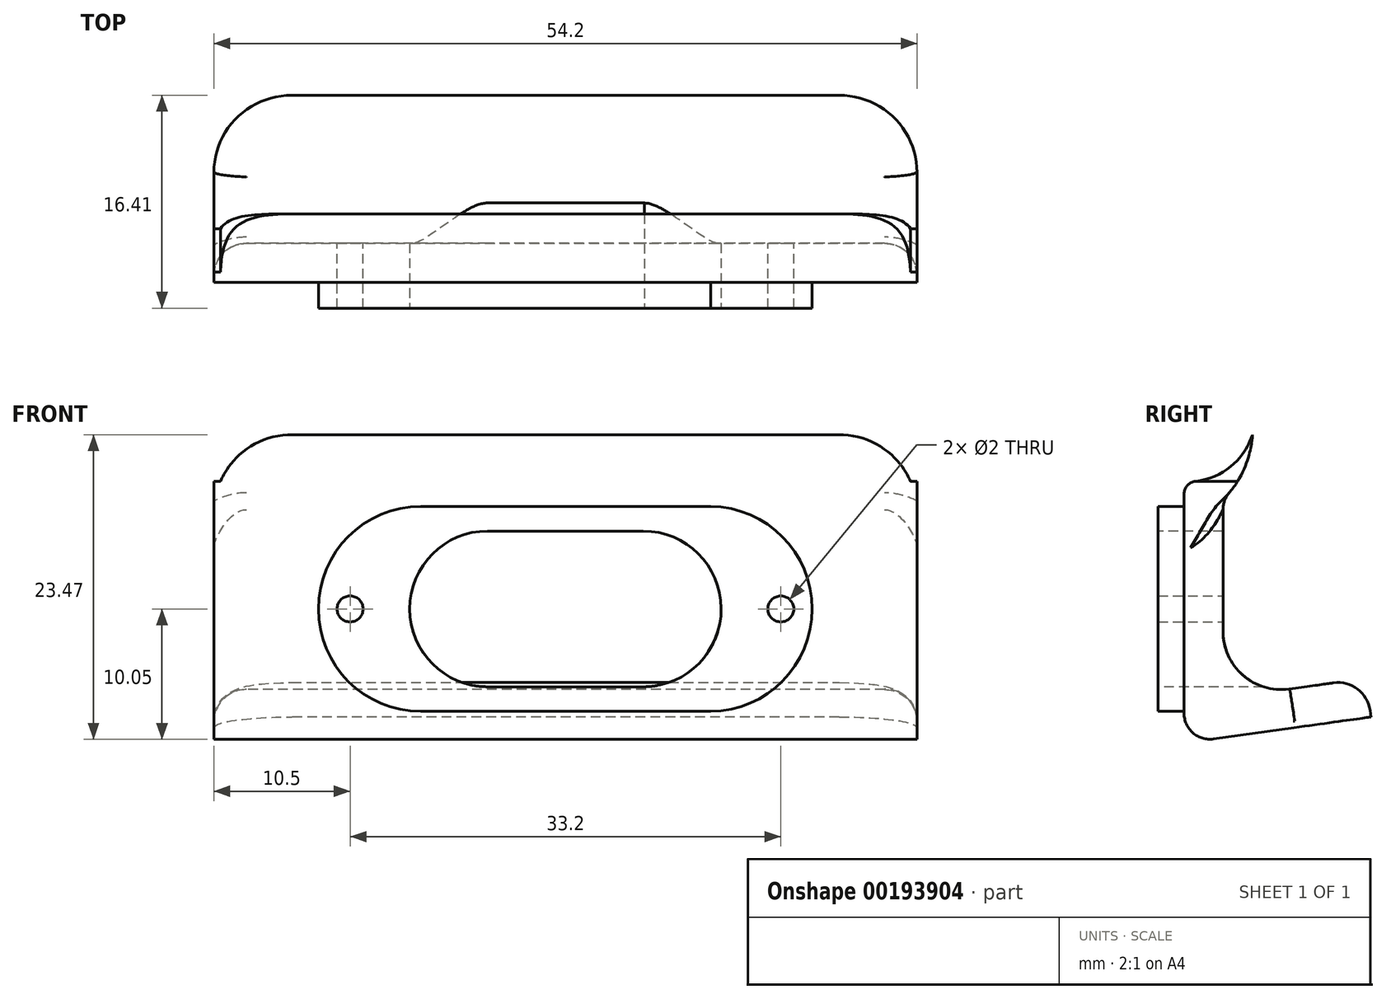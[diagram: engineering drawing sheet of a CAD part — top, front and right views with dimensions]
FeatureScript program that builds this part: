
annotation { "Feature Type Name" : "Feature", "Feature Type Description" : "" }
export const myFeature = defineFeature(function(context is Context, id is Id, definition is map)
    precondition{}
    {
        {
            var Q0;
            Q0=qCreatedBy(makeId("Front.planeOp"),FACE);
            var sketch = newSketch(context, id + "F0", { "sketchPlane" : qUnion([Q0])});
            skLineSegment(sketch, "E0", {"start": v(-6, -6) * mm, "end": v(6.1, -6) * mm});
            skPoint(sketch, "E1.endSnap0", {"position": v(0.05, -6) * mm});
            skArc(sketch, "E2", {"start": v(-11.14, 7.9) * mm, "mid": v(-19.04, 0) * mm, "end": v(-11.14, -7.9) * mm});
            skArc(sketch, "E3", {"start": v(11.2, -7.9) * mm, "mid": v(19.02, 0) * mm, "end": v(11.2, 7.9) * mm});
            skLineSegment(sketch, "E4", {"start": v(-11.14, 7.9) * mm, "end": v(11.2, 7.9) * mm});
            skLineSegment(sketch, "E5", {"start": v(-11.14, -7.9) * mm, "end": v(11.2, -7.9) * mm});
            skPoint(sketch, "E6", {"position": v(0.03, 7.9) * mm});
            skPoint(sketch, "E7", {"position": v(0, 15.9) * mm});
            skPoint(sketch, "E8", {"position": v(0.05, -7.9) * mm});
            skPoint(sketch, "E9", {"position": v(0.05, -10.36) * mm});
            skPoint(sketch, "E10", {"position": v(19.02, 0) * mm});
            skPoint(sketch, "E11", {"position": v(27.02, 0) * mm});
            skPoint(sketch, "E12", {"position": v(-19.04, 0) * mm});
            skPoint(sketch, "E13", {"position": v(-27.04, 0) * mm});
            skLineSegment(sketch, "E14", {"start": v(27.02, 0) * mm, "end": v(11.12, 0) * mm, "construction": true});
            skLineSegment(sketch, "E15", {"start": v(-27.04, 0) * mm, "end": v(-11.14, 0) * mm, "construction": true});
            skLineSegment(sketch, "E16", {"start": v(27.02, 0) * mm, "end": v(27.02, -10.36) * mm});
            skLineSegment(sketch, "E17", {"start": v(27.02, -10.36) * mm, "end": v(0.05, -10.36) * mm});
            skLineSegment(sketch, "E18", {"start": v(-27.04, 0) * mm, "end": v(-27.04, -10.36) * mm});
            skLineSegment(sketch, "E19", {"start": v(-27.04, -10.36) * mm, "end": v(0.05, -10.36) * mm});
            skLineSegment(sketch, "E20", {"start": v(-6, -6) * mm, "end": v(-6, 6) * mm, "construction": true});
            skArc(sketch, "E21", {"start": v(-6, 6) * mm, "mid": v(-12, 0) * mm, "end": v(-6, -6) * mm});
            skLineSegment(sketch, "E22", {"start": v(6, 6) * mm, "end": v(-6, 6) * mm});
            skArc(sketch, "E23", {"start": v(6.1, -6) * mm, "mid": v(12, 0.05) * mm, "end": v(6, 6) * mm});
            skLineSegment(sketch, "E24", {"start": v(0, 2.4) * mm, "end": v(16.6, 2.4) * mm, "construction": true});
            skLineSegment(sketch, "E25", {"start": v(16.6, 2.4) * mm, "end": v(16.6, 0) * mm, "construction": true});
            skLineSegment(sketch, "E26.MirrorCS", {"start": v(16.6, 2.4) * mm, "end": v(16.6, 4.8) * mm, "construction": true});
            skLineSegment(sketch, "E27.MirrorCS", {"start": v(-16.6, 2.4) * mm, "end": v(-16.6, 0) * mm, "construction": true});
            skCircle(sketch, "E28", {"center": v(-16.6, 0) * mm, "radius": 1 * mm});
            skCircle(sketch, "E29", {"center": v(16.6, 0) * mm, "radius": 1 * mm});
            skPoint(sketch, "E30.0.midPoint", {"position": v(16.6, -2.75) * mm});
            skPoint(sketch, "E31.0.midPoint", {"position": v(-16.6, -2.75) * mm});
            skSolve(sketch);
        }
        {
            var Q0;
            Q0=qCreatedBy(makeId("Right.planeOp"),FACE);
            var sketch = newSketch(context, id + "F1", { "sketchPlane" : qUnion([Q0])});
            skPoint(sketch, "E32", {"position": v(-15.3, 23.66) * mm});
            skLineSegment(sketch, "E33", {"start": v(0, 0) * mm, "end": v(16.18, 0) * mm, "construction": true});
            skLineSegment(sketch, "E34", {"start": v(16.18, 0) * mm, "end": v(16.18, 14.83) * mm, "construction": true});
            skLineSegment(sketch, "E35", {"start": v(16.18, 14.83) * mm, "end": v(-20.13, 14.83) * mm, "construction": true});
            skLineSegment(sketch, "E36", {"start": v(0, 19.1) * mm, "end": v(0.5, 19.1) * mm, "construction": true});
            skLineSegment(sketch, "E37", {"start": v(0.5, 19.1) * mm, "end": v(0.5, 14.83) * mm, "construction": true});
            skArc(sketch, "E38", {"start": v(0.5, 9.83) * mm, "mid": v(0.68, 9.83) * mm, "end": v(0.86, 9.84) * mm});
            skArc(sketch, "E39", {"start": v(0, 9.83) * mm, "mid": v(3.82, 11.16) * mm, "end": v(5.5, 14.83) * mm});
            skLineSegment(sketch, "E40", {"start": v(0, 9.83) * mm, "end": v(0, 7.9) * mm});
            skLineSegment(sketch, "E41", {"start": v(0, 7.9) * mm, "end": v(-2, 7.9) * mm});
            skLineSegment(sketch, "E42", {"start": v(-2, 7.9) * mm, "end": v(-2, 5.99) * mm});
            skArc(sketch, "E43.trimOffspring", {"start": v(5.5, 14.83) * mm, "mid": v(5.43, 15.63) * mm, "end": v(5.24, 16.41) * mm});
            skLineSegment(sketch, "E44", {"start": v(0, 9.83) * mm, "end": v(0.5, 9.83) * mm});
            skCircle(sketch, "E45", {"center": v(0.35, 14.97) * mm, "radius": 5.15 * mm, "construction": true});
            skLineSegment(sketch, "E46", {"start": v(0, 0) * mm, "end": v(0, -3.97) * mm});
            skPoint(sketch, "E47.visualSharp", {"position": v(0, -10.35) * mm});
            skLineSegment(sketch, "E48", {"start": v(3, -9.92) * mm, "end": v(14.41, -8.32) * mm});
            skPoint(sketch, "E49.visualSharp", {"position": v(14, -5.35) * mm});
            skLineSegment(sketch, "E50", {"start": v(3, -6.9) * mm, "end": v(3, 0) * mm});
            skPoint(sketch, "E51.start.orphan", {"position": v(0, -7.85) * mm});
            skLineSegment(sketch, "E52", {"start": v(3, -9.92) * mm, "end": v(0, -10.35) * mm});
            skLineSegment(sketch, "E53", {"start": v(0, -10.35) * mm, "end": v(0, -7.85) * mm});
            skLineSegment(sketch, "E54", {"start": v(0, -7.85) * mm, "end": v(0, 0) * mm});
            skLineSegment(sketch, "E55", {"start": v(0, 0) * mm, "end": v(3, 0) * mm});
            skLineSegment(sketch, "E56", {"start": v(3, -6.9) * mm, "end": v(14, -5.35) * mm});
            skLineSegment(sketch, "E57", {"start": v(14.41, -8.32) * mm, "end": v(14, -5.35) * mm});
            skLineSegment(sketch, "E58", {"start": v(0, 0) * mm, "end": v(3, 0) * mm, "construction": true});
            skLineSegment(sketch, "E59", {"start": v(0.5, 9.83) * mm, "end": v(0.5, 6.83) * mm, "construction": true});
            skPoint(sketch, "E60", {"position": v(5.27, 13.43) * mm});
            skArc(sketch, "E61", {"start": v(0.5, 6.83) * mm, "mid": v(0.68, 6.9) * mm, "end": v(0.87, 6.98) * mm});
            skLineSegment(sketch, "E62", {"start": v(3, 0) * mm, "end": v(3, 8.44) * mm});
            skArc(sketch, "E63.trimOffspring", {"start": v(3, 8.44) * mm, "mid": v(4.6, 10.72) * mm, "end": v(5.27, 13.43) * mm});
            skLineSegment(sketch, "E64", {"start": v(0, 7.9) * mm, "end": v(0, 0) * mm});
            skSolve(sketch);
        }
        {
            var Q0;
            Q0=makeQuery(id+"F1.imprint","IMPRINT",FACE,{"disambiguationData":[TD([[makeQuery(id+"F1.imprint","IMPRINT",EDGE,{"derivedFrom":sQuery(id+"F1.wireOp",EDGE,"E48")}),1.0]])]});
            var Q1;
            {var subQ5=sQuery(id+"F1.wireOp",EDGE,"E40");Q1=makeQuery(id+"F1.imprint","IMPRINT",FACE,{"disambiguationData":[TD([[makeQuery(id+"F1.imprint","IMPRINT",EDGE,{"derivedFrom":subQ5}),1.0]])]});}
            extrude(context, id + "F2", {"entities" : qUnion([Q0, Q1]), "endBound" : BoundingType.SYMMETRIC, "depth" : 54.2 * mm});
        }
        {
            var Q0;
            Q0=makeQuery(id+"F0.imprint","IMPRINT",FACE,{"disambiguationData":[TD([[makeQuery(id+"F0.imprint","IMPRINT",EDGE,{"derivedFrom":sQuery(id+"F0.wireOp",EDGE,"E0")}),1.0]])]});
            extrude(context, id + "F3", {"entities" : qUnion([Q0]), "operationType" : NewBodyOperationType.ADD, "oppositeDirection" : true, "depth" : 3 * mm});
        }
        {
            var Q0;
            Q0=makeQuery(id+"F0.imprint","IMPRINT",FACE,{"disambiguationData":[TD([[makeQuery(id+"F0.imprint","IMPRINT",EDGE,{"derivedFrom":sQuery(id+"F0.wireOp",EDGE,"E0")}),1.0]])]});
            extrude(context, id + "F4", {"entities" : qUnion([Q0]), "operationType" : NewBodyOperationType.REMOVE, "oppositeDirection" : true, "depth" : 3 * mm});
        }
        {
            var Q0;
            Q0=makeQuery(id+"F0.imprint","IMPRINT",FACE,{"disambiguationData":[TD([[makeQuery(id+"F0.imprint","IMPRINT",EDGE,{"derivedFrom":sQuery(id+"F0.wireOp",EDGE,"E0")}),-1.0]])]});
            extrude(context, id + "F5", {"entities" : qUnion([Q0]), "operationType" : NewBodyOperationType.ADD, "depth" : 2 * mm});
        }
        {
            var Q0;
            Q0=makeQuery(id+"F2.opExtrude","SWEPT_EDGE",EDGE,{"disambiguationData":[OSD([sQuery(id+"F1.wireOp",EDGE,"E50"),sQuery(id+"F1.wireOp",EDGE,"E56")])]});
            var Q1;
            Q1=makeQuery(id+"F4.boolean.opBoolean","COPY",EDGE,{"derivedFrom":makeQuery(id+"F4.opExtrude","CAP_EDGE",EDGE,{"disambiguationData":[OSD([sQuery(id+"F0.wireOp",EDGE,"E22")])],"isStart":false})});
            fillet(context, id + "F6", {"entities" : qUnion([Q0, Q1]), "radius" : 4.5 * mm, "tangentPropagation" : true, "allowEdgeOverflow" : false});
        }
        {
            var Q0;
            Q0=makeQuery(id+"F2.opExtrude","SWEPT_FACE",FACE,{"disambiguationData":[OSD([sQuery(id+"F1.wireOp",EDGE,"E48"),sQuery(id+"F1.wireOp",EDGE,"E52")])]});
            var sketch = newSketch(context, id + "F7", { "sketchPlane" : qUnion([Q0])});
            skLineSegment(sketch, "E65", {"start": v(27.1, -7.11) * mm, "end": v(27.1, -7.11) * mm});
            skLineSegment(sketch, "E66", {"start": v(21.1, -13.11) * mm, "end": v(21.1, -13.11) * mm});
            skLineSegment(sketch, "E67", {"start": v(27.1, -7.11) * mm, "end": v(21.1, -7.11) * mm, "construction": true});
            skPoint(sketch, "E68.visualSharp", {"position": v(27.1, -13.11) * mm});
            skArc(sketch, "E68.filletArc", {"start": v(21.1, -13.11) * mm, "mid": v(25.34, -11.36) * mm, "end": v(27.1, -7.11) * mm});
            skLineSegment(sketch, "E69", {"start": v(27.1, -7.11) * mm, "end": v(27.1, -13.11) * mm});
            skLineSegment(sketch, "E70", {"start": v(21.1, -13.11) * mm, "end": v(27.1, -13.11) * mm});
            skLineSegment(sketch, "E71", {"start": v(-27.1, -7.11) * mm, "end": v(-27.1, -7.11) * mm});
            skLineSegment(sketch, "E72", {"start": v(-21.1, -13.11) * mm, "end": v(-21.1, -13.11) * mm});
            skLineSegment(sketch, "E73", {"start": v(-21.1, -13.11) * mm, "end": v(-21.1, -7.11) * mm, "construction": true});
            skLineSegment(sketch, "E74", {"start": v(-21.1, -7.11) * mm, "end": v(-27.1, -7.11) * mm, "construction": true});
            skPoint(sketch, "E75.visualSharp", {"position": v(-27.1, -13.11) * mm});
            skArc(sketch, "E75.filletArc", {"start": v(-27.1, -7.11) * mm, "mid": v(-25.34, -11.36) * mm, "end": v(-21.1, -13.11) * mm});
            skSolve(sketch);
        }
        {
            var Q0;
            Q0=makeQuery(id+"F7.imprint","IMPRINT",FACE,{"disambiguationData":[TD([[makeQuery(id+"F7.imprint","IMPRINT",EDGE,{"derivedFrom":sQuery(id+"F7.wireOp",EDGE,"E68.filletArc")}),-1.0]])]});
            extrude(context, id + "F8", {"entities" : qUnion([Q0]), "operationType" : NewBodyOperationType.REMOVE, "oppositeDirection" : true, "depth" : 3 * mm});
        }
        {
            var Q0;
            {var subQ0=sQuery(id+"F7.wireOp",EDGE,"E75.filletArc");Q0=makeQuery(id+"F7.imprint","IMPRINT",FACE,{"disambiguationData":[TD([[makeQuery(id+"F7.imprint","IMPRINT",EDGE,{"derivedFrom":subQ0}),-1.0]])]});}
            extrude(context, id + "F9", {"entities" : qUnion([Q0]), "operationType" : NewBodyOperationType.REMOVE, "oppositeDirection" : true, "depth" : 3 * mm});
        }
        {
            var Q0;
            {var subQ0=sQuery(id+"F1.wireOp",EDGE,"E56");var subQ1=sQuery(id+"F1.wireOp",EDGE,"E50");Q0=makeQuery(id+"F8.boolean.opBoolean","SPLIT",EDGE,{"derivedFrom":makeQuery(id+"F6.opFillet","BLEND_EDGE",EDGE,{"blendedFrom":[makeQuery(id+"F2.opExtrude","SWEPT_EDGE",EDGE,{"disambiguationData":[OSD([subQ1,subQ0])]}),makeQuery(id+"F2.opExtrude","CAP_FACE",FACE,{"disambiguationData":[OSD([sQuery(id+"F1.wireOp",EDGE,"E39"),sQuery(id+"F1.wireOp",EDGE,"E40"),sQuery(id+"F1.wireOp",EDGE,"E48"),subQ1,sQuery(id+"F1.wireOp",EDGE,"E52"),sQuery(id+"F1.wireOp",EDGE,"E53"),sQuery(id+"F1.wireOp",EDGE,"E54"),subQ0,sQuery(id+"F1.wireOp",EDGE,"E57"),sQuery(id+"F1.wireOp",EDGE,"E62"),sQuery(id+"F1.wireOp",EDGE,"E63.trimOffspring"),sQuery(id+"F1.wireOp",EDGE,"E64")])],"isStart":false})],"blendedInto":[makeQuery(id+"F2.opExtrude","CAP_FACE",FACE,{"disambiguationData":[OSD([sQuery(id+"F1.wireOp",EDGE,"E39"),sQuery(id+"F1.wireOp",EDGE,"E40"),sQuery(id+"F1.wireOp",EDGE,"E48"),subQ1,sQuery(id+"F1.wireOp",EDGE,"E52"),sQuery(id+"F1.wireOp",EDGE,"E53"),sQuery(id+"F1.wireOp",EDGE,"E54"),subQ0,sQuery(id+"F1.wireOp",EDGE,"E57"),sQuery(id+"F1.wireOp",EDGE,"E62"),sQuery(id+"F1.wireOp",EDGE,"E63.trimOffspring"),sQuery(id+"F1.wireOp",EDGE,"E64")])],"isStart":false})]})});}
            var Q1;
            Q1=makeQuery(id+"F8.boolean.opBoolean","COPY",EDGE,{"derivedFrom":makeQuery(id+"F8.opExtrude","CAP_EDGE",EDGE,{"disambiguationData":[OSD([sQuery(id+"F7.wireOp",EDGE,"E68.filletArc")])],"isStart":false})});
            var Q2;
            Q2=makeQuery(id+"F2.opExtrude","SWEPT_EDGE",EDGE,{"disambiguationData":[OSD([sQuery(id+"F1.wireOp",EDGE,"E56"),sQuery(id+"F1.wireOp",EDGE,"E57")])]});
            var Q3;
            Q3=makeQuery(id+"F9.boolean.opBoolean","COPY",EDGE,{"derivedFrom":makeQuery(id+"F9.opExtrude","CAP_EDGE",EDGE,{"disambiguationData":[OSD([sQuery(id+"F7.wireOp",EDGE,"E75.filletArc")])],"isStart":false})});
            var Q4;
            {var subQ0=sQuery(id+"F1.wireOp",EDGE,"E56");var subQ1=sQuery(id+"F1.wireOp",EDGE,"E50");Q4=makeQuery(id+"F9.boolean.opBoolean","SPLIT",EDGE,{"derivedFrom":makeQuery(id+"F6.opFillet","BLEND_EDGE",EDGE,{"blendedFrom":[makeQuery(id+"F2.opExtrude","SWEPT_EDGE",EDGE,{"disambiguationData":[OSD([subQ1,subQ0])]}),makeQuery(id+"F2.opExtrude","CAP_FACE",FACE,{"disambiguationData":[OSD([sQuery(id+"F1.wireOp",EDGE,"E39"),sQuery(id+"F1.wireOp",EDGE,"E40"),sQuery(id+"F1.wireOp",EDGE,"E48"),subQ1,sQuery(id+"F1.wireOp",EDGE,"E52"),sQuery(id+"F1.wireOp",EDGE,"E53"),sQuery(id+"F1.wireOp",EDGE,"E54"),subQ0,sQuery(id+"F1.wireOp",EDGE,"E57"),sQuery(id+"F1.wireOp",EDGE,"E62"),sQuery(id+"F1.wireOp",EDGE,"E63.trimOffspring"),sQuery(id+"F1.wireOp",EDGE,"E64")])],"isStart":true})],"blendedInto":[makeQuery(id+"F2.opExtrude","CAP_FACE",FACE,{"disambiguationData":[OSD([sQuery(id+"F1.wireOp",EDGE,"E39"),sQuery(id+"F1.wireOp",EDGE,"E40"),sQuery(id+"F1.wireOp",EDGE,"E48"),subQ1,sQuery(id+"F1.wireOp",EDGE,"E52"),sQuery(id+"F1.wireOp",EDGE,"E53"),sQuery(id+"F1.wireOp",EDGE,"E54"),subQ0,sQuery(id+"F1.wireOp",EDGE,"E57"),sQuery(id+"F1.wireOp",EDGE,"E62"),sQuery(id+"F1.wireOp",EDGE,"E63.trimOffspring"),sQuery(id+"F1.wireOp",EDGE,"E64")])],"isStart":true})]})});}
            fillet(context, id + "F10", {"entities" : qUnion([Q0, Q1, Q2, Q3, Q4]), "radius" : 2.5 * mm, "tangentPropagation" : true, "allowEdgeOverflow" : false});
        }
        {
            var Q0;
            Q0=makeQuery(id+"F2.opExtrude","SWEPT_FACE",FACE,{"disambiguationData":[OSD([sQuery(id+"F1.wireOp",EDGE,"E40"),sQuery(id+"F1.wireOp",EDGE,"E53"),sQuery(id+"F1.wireOp",EDGE,"E54"),sQuery(id+"F1.wireOp",EDGE,"E64")])]});
            var sketch = newSketch(context, id + "F11", { "sketchPlane" : qUnion([Q0])});
            skLineSegment(sketch, "E76", {"start": v(27.1, 0) * mm, "end": v(21.1, 0) * mm, "construction": true});
            skLineSegment(sketch, "E77", {"start": v(-27.1, 0) * mm, "end": v(-11.15, 0) * mm, "construction": true});
            skPoint(sketch, "E77.startSnap0", {"position": v(-19.04, 0) * mm});
            skLineSegment(sketch, "E78", {"start": v(21.1, 13.43) * mm, "end": v(27.1, 13.43) * mm});
            skLineSegment(sketch, "E79", {"start": v(27.1, 13.43) * mm, "end": v(27.1, 7.43) * mm});
            skArc(sketch, "E80", {"start": v(27.1, 7.43) * mm, "mid": v(25.34, 11.67) * mm, "end": v(21.1, 13.43) * mm});
            skLineSegment(sketch, "E81.MirrorCS", {"start": v(-21.1, 13.43) * mm, "end": v(-27.1, 13.43) * mm});
            skLineSegment(sketch, "E82.MirrorCS", {"start": v(-27.1, 13.43) * mm, "end": v(-27.1, 7.43) * mm});
            skArc(sketch, "E83", {"start": v(-21.1, 13.43) * mm, "mid": v(-25.34, 11.67) * mm, "end": v(-27.1, 7.43) * mm});
            skSolve(sketch);
        }
        {
            var Q0;
            {var subQ0=sQuery(id+"F11.wireOp",EDGE,"E79");var subQ1=sQuery(id+"F1.wireOp",EDGE,"E40");var subQ4=sQuery(id+"F11.wireOp",EDGE,"E80");var subQ5=makeQuery(id+"F11.imprint","INTERSECT",VERTEX,{"derivedFrom":[makeQuery(id+"F2.opExtrude","CAP_EDGE",EDGE,{"disambiguationData":[OSD([subQ1,sQuery(id+"F1.wireOp",EDGE,"E53"),sQuery(id+"F1.wireOp",EDGE,"E54"),sQuery(id+"F1.wireOp",EDGE,"E64")])],"isStart":false}),subQ0,subQ4]});Q0=makeQuery(id+"F11.imprint","IMPRINT",FACE,{"disambiguationData":[TD([[makeQuery(id+"F11.imprint","IMPRINT",EDGE,{"disambiguationData":[TD([[subQ5,-1.0]])],"derivedFrom":subQ0}),1.0]])]});}
            var Q1;
            {var subQ0=sQuery(id+"F11.wireOp",EDGE,"E78");Q1=makeQuery(id+"F11.imprint","IMPRINT",FACE,{"disambiguationData":[TD([[makeQuery(id+"F11.imprint","IMPRINT",EDGE,{"derivedFrom":subQ0}),-1.0]])]});}
            extrude(context, id + "F12", {"entities" : qUnion([Q0, Q1]), "operationType" : NewBodyOperationType.REMOVE, "oppositeDirection" : true, "depth" : 25 * mm});
        }
        {
            var Q0;
            {var subQ0=sQuery(id+"F11.wireOp",EDGE,"E81.MirrorCS");Q0=makeQuery(id+"F11.imprint","IMPRINT",FACE,{"disambiguationData":[TD([[makeQuery(id+"F11.imprint","IMPRINT",EDGE,{"derivedFrom":subQ0}),1.0]])]});}
            var Q1;
            {var subQ0=sQuery(id+"F11.wireOp",EDGE,"E82.MirrorCS");var subQ1=sQuery(id+"F1.wireOp",EDGE,"E40");var subQ4=sQuery(id+"F11.wireOp",EDGE,"E83");var subQ5=makeQuery(id+"F11.imprint","INTERSECT",VERTEX,{"derivedFrom":[makeQuery(id+"F2.opExtrude","CAP_EDGE",EDGE,{"disambiguationData":[OSD([subQ1,sQuery(id+"F1.wireOp",EDGE,"E53"),sQuery(id+"F1.wireOp",EDGE,"E54"),sQuery(id+"F1.wireOp",EDGE,"E64")])],"isStart":true}),subQ0,subQ4]});Q1=makeQuery(id+"F11.imprint","IMPRINT",FACE,{"disambiguationData":[TD([[makeQuery(id+"F11.imprint","IMPRINT",EDGE,{"disambiguationData":[TD([[subQ5,-1.0]])],"derivedFrom":subQ0}),-1.0]])]});}
            extrude(context, id + "F13", {"entities" : qUnion([Q0, Q1]), "operationType" : NewBodyOperationType.REMOVE, "oppositeDirection" : true, "depth" : 25 * mm});
        }
        {
            var Q0;
            Q0=makeQuery(id+"F2.opExtrude","SWEPT_EDGE",EDGE,{"disambiguationData":[OSD([sQuery(id+"F1.wireOp",EDGE,"E52"),sQuery(id+"F1.wireOp",EDGE,"E53")])]});
            fillet(context, id + "F14", {"entities" : qUnion([Q0]), "radius" : 2 * mm, "tangentPropagation" : true, "allowEdgeOverflow" : false});
        }
        {
            var Q0;
            Q0=makeQuery(id+"F2.opExtrude","SWEPT_EDGE",EDGE,{"disambiguationData":[OSD([sQuery(id+"F1.wireOp",EDGE,"E39"),sQuery(id+"F1.wireOp",EDGE,"E40"),sQuery(id+"F1.wireOp",EDGE,"E44")])]});
            fillet(context, id + "F15", {"entities" : qUnion([Q0]), "radius" : 1 * mm, "tangentPropagation" : true, "allowEdgeOverflow" : false});
        }
        {
            var Q0;
            Q0=makeQuery(id+"F0.imprint","IMPRINT",FACE,{"disambiguationData":[TD([[makeQuery(id+"F0.imprint","IMPRINT",EDGE,{"derivedFrom":sQuery(id+"F0.wireOp",EDGE,"E28")}),1.0]])]});
            var Q1;
            Q1=makeQuery(id+"F0.imprint","IMPRINT",FACE,{"disambiguationData":[TD([[makeQuery(id+"F0.imprint","IMPRINT",EDGE,{"derivedFrom":sQuery(id+"F0.wireOp",EDGE,"E29")}),1.0]])]});
            extrude(context, id + "F16", {"entities" : qUnion([Q0, Q1]), "operationType" : NewBodyOperationType.REMOVE, "endBound" : BoundingType.SYMMETRIC, "depth" : 10 * mm});
        }
        {
            var Q0;
            Q0=makeQuery(id+"F10.opFillet","BLEND_EDGE",EDGE,{"blendedFrom":[makeQuery(id+"F2.opExtrude","CAP_EDGE",EDGE,{"disambiguationData":[OSD([sQuery(id+"F1.wireOp",EDGE,"E50"),sQuery(id+"F1.wireOp",EDGE,"E62")])],"isStart":false}),makeQuery(id+"F2.opExtrude","SWEPT_FACE",FACE,{"disambiguationData":[OSD([sQuery(id+"F1.wireOp",EDGE,"E63.trimOffspring")])]})],"blendedInto":[makeQuery(id+"F2.opExtrude","SWEPT_FACE",FACE,{"disambiguationData":[OSD([sQuery(id+"F1.wireOp",EDGE,"E63.trimOffspring")])]})]});
            var Q1;
            Q1=makeQuery(id+"F2.opExtrude","SWEPT_EDGE",EDGE,{"disambiguationData":[OSD([sQuery(id+"F1.wireOp",EDGE,"E62"),sQuery(id+"F1.wireOp",EDGE,"E63.trimOffspring")])]});
            var Q2;
            Q2=makeQuery(id+"F6.opFillet","BLEND_EDGE",EDGE,{"blendedFrom":[makeQuery(id+"F4.boolean.opBoolean","COPY",EDGE,{"derivedFrom":makeQuery(id+"F4.opExtrude","CAP_EDGE",EDGE,{"disambiguationData":[OSD([sQuery(id+"F0.wireOp",EDGE,"E23")])],"isStart":false})}),makeQuery(id+"F2.opExtrude","SWEPT_FACE",FACE,{"disambiguationData":[OSD([sQuery(id+"F1.wireOp",EDGE,"E63.trimOffspring")])]})],"blendedInto":[makeQuery(id+"F2.opExtrude","SWEPT_FACE",FACE,{"disambiguationData":[OSD([sQuery(id+"F1.wireOp",EDGE,"E63.trimOffspring")])]})]});
            var Q3;
            Q3=makeQuery(id+"F6.opFillet","BLEND_EDGE",EDGE,{"disambiguationData":[OD(0.0)],"blendedFrom":[makeQuery(id+"F4.boolean.opBoolean","COPY",EDGE,{"derivedFrom":makeQuery(id+"F4.opExtrude","CAP_EDGE",EDGE,{"disambiguationData":[OSD([sQuery(id+"F0.wireOp",EDGE,"E21")])],"isStart":false})}),makeQuery(id+"F2.opExtrude","SWEPT_FACE",FACE,{"disambiguationData":[OSD([sQuery(id+"F1.wireOp",EDGE,"E63.trimOffspring")])]})],"blendedInto":[makeQuery(id+"F2.opExtrude","SWEPT_FACE",FACE,{"disambiguationData":[OSD([sQuery(id+"F1.wireOp",EDGE,"E63.trimOffspring")])]})]});
            var Q4;
            Q4=makeQuery(id+"F6.opFillet","BLEND_EDGE",EDGE,{"disambiguationData":[OD(1.0)],"blendedFrom":[makeQuery(id+"F4.boolean.opBoolean","COPY",EDGE,{"derivedFrom":makeQuery(id+"F4.opExtrude","CAP_EDGE",EDGE,{"disambiguationData":[OSD([sQuery(id+"F0.wireOp",EDGE,"E21")])],"isStart":false})}),makeQuery(id+"F2.opExtrude","SWEPT_FACE",FACE,{"disambiguationData":[OSD([sQuery(id+"F1.wireOp",EDGE,"E63.trimOffspring")])]})],"blendedInto":[makeQuery(id+"F2.opExtrude","SWEPT_FACE",FACE,{"disambiguationData":[OSD([sQuery(id+"F1.wireOp",EDGE,"E63.trimOffspring")])]})]});
            var Q5;
            Q5=makeQuery(id+"F2.opExtrude","SWEPT_EDGE",EDGE,{"disambiguationData":[OSD([sQuery(id+"F1.wireOp",EDGE,"E62"),sQuery(id+"F1.wireOp",EDGE,"E63.trimOffspring")])]});
            var Q6;
            Q6=makeQuery(id+"F10.opFillet","BLEND_EDGE",EDGE,{"blendedFrom":[makeQuery(id+"F2.opExtrude","CAP_EDGE",EDGE,{"disambiguationData":[OSD([sQuery(id+"F1.wireOp",EDGE,"E50"),sQuery(id+"F1.wireOp",EDGE,"E62")])],"isStart":true}),makeQuery(id+"F2.opExtrude","SWEPT_FACE",FACE,{"disambiguationData":[OSD([sQuery(id+"F1.wireOp",EDGE,"E63.trimOffspring")])]})],"blendedInto":[makeQuery(id+"F2.opExtrude","SWEPT_FACE",FACE,{"disambiguationData":[OSD([sQuery(id+"F1.wireOp",EDGE,"E63.trimOffspring")])]})]});
            fillet(context, id + "F17", {"entities" : qUnion([Q0, Q1, Q2, Q3, Q4, Q5, Q6]), "radius" : 2 * mm, "tangentPropagation" : true, "allowEdgeOverflow" : false});
        }
    });
